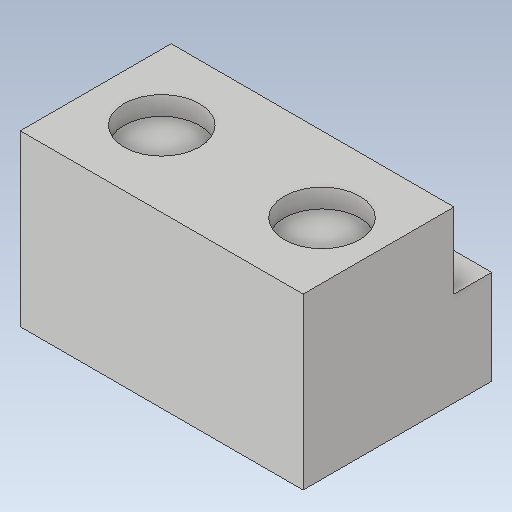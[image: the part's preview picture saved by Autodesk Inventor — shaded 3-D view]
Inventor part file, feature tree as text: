
AUTODESK INVENTOR PART (.ipt)
format: ipt  version: 2020 (Build 240168000, 168)  size: 122,880 bytes
history: native  units: mm
features: extrude x3, sketch x3, other x1
ambient origin geometry x8: Origin, YZ Plane, XZ Plane, XY Plane, X Axis, Y Axis, Z Axis, Center Point
bodies: Body1 (feature_tree)
feature tree (7):
  other  "Bryła1"
  extrude  "Wyciągnięcie proste1"  Depth=10.0mm
  extrude  "Wyciągnięcie proste2"  Depth=15.0mm
  extrude  "Wyciągnięcie proste3"  Depth=5.0mm
  sketch  "Szkic1"
  sketch  "Szkic2"
  sketch  "Szkic3"
